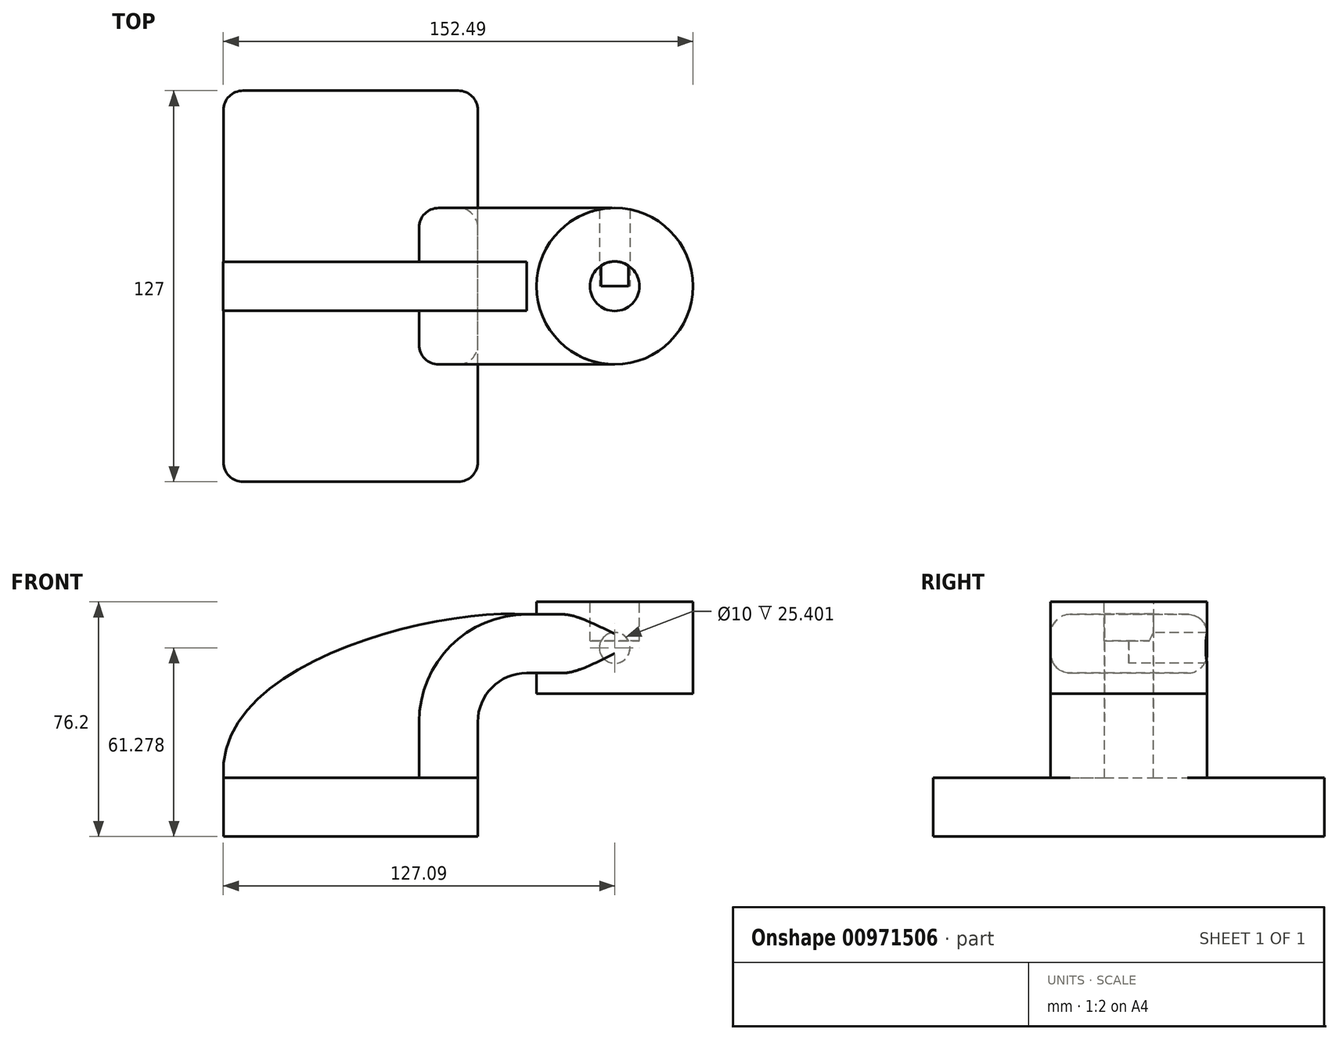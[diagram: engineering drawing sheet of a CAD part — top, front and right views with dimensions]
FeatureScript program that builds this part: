
annotation { "Feature Type Name" : "Feature", "Feature Type Description" : "" }
export const myFeature = defineFeature(function(context is Context, id is Id, definition is map)
    precondition{}
    {
        {
            var Q0;
            Q0=qCreatedBy(makeId("Front.planeOp"),FACE);
            var sketch = newSketch(context, id + "F0", { "sketchPlane" : qUnion([Q0])});
            skLineSegment(sketch, "E0.bottom", {"start": v(0, 0) * mm, "end": v(-82.55, 0) * mm});
            skLineSegment(sketch, "E0.top", {"start": v(0, 19.05) * mm, "end": v(-82.55, 19.05) * mm});
            skLineSegment(sketch, "E0.left", {"start": v(0, 0) * mm, "end": v(0, 19.05) * mm});
            skLineSegment(sketch, "E0.right", {"start": v(-82.55, 0) * mm, "end": v(-82.55, 19.05) * mm});
            skLineSegment(sketch, "E1", {"start": v(0, 19.05) * mm, "end": v(0, 37.22) * mm});
            skArc(sketch, "E2", {"start": v(15.88, 53.1) * mm, "mid": v(4.65, 48.44) * mm, "end": v(0, 37.22) * mm});
            skLineSegment(sketch, "E3", {"start": v(15.88, 53.1) * mm, "end": v(64.16, 53.1) * mm});
            skLineSegment(sketch, "E4.bottom", {"start": v(69.85, 46.35) * mm, "end": v(19.05, 46.35) * mm});
            skLineSegment(sketch, "E4.top", {"start": v(69.85, 76.2) * mm, "end": v(19.05, 76.2) * mm});
            skLineSegment(sketch, "E4.left", {"start": v(69.85, 46.35) * mm, "end": v(69.85, 76.2) * mm});
            skLineSegment(sketch, "E4.right", {"start": v(19.05, 46.35) * mm, "end": v(19.05, 76.2) * mm});
            skPoint(sketch, "E4.middle", {"position": v(44.45, 61.28) * mm});
            skLineSegment(sketch, "E5.0", {"start": v(15.88, 72.14) * mm, "end": v(64.16, 72.14) * mm});
            skArc(sketch, "E5.1", {"start": v(15.88, 72.14) * mm, "mid": v(-8.82, 61.91) * mm, "end": v(-19.05, 37.22) * mm});
            skLineSegment(sketch, "E5.2", {"start": v(-19.05, 19.05) * mm, "end": v(-19.05, 37.22) * mm});
            skLineSegment(sketch, "E6", {"start": v(44.45, 46.35) * mm, "end": v(44.45, 76.2) * mm});
            skFitSpline(sketch, "E7", {"points": [v(-82.55, 19.05) * mm, v(15.88, 72.14) * mm], "startDerivative": vector(-9.17, 113.87) * mm, "endDerivative": vector(84.95, -6.67) * mm});
            skSolve(sketch);
        }
        {
            var Q0;
            Q0=makeQuery(id+"F0.imprint","IMPRINT",FACE,{"disambiguationData":[TD([[makeQuery(id+"F0.imprint","IMPRINT",EDGE,{"derivedFrom":sQuery(id+"F0.wireOp",EDGE,"E0.bottom")}),-1.0]])]});
            extrude(context, id + "F1", {"entities" : qUnion([Q0]), "endBound" : BoundingType.SYMMETRIC, "depth" : 127 * mm, "offsetDistance" : 25.4 * mm});
        }
        {
            var Q0;
            {var subQ4=sQuery(id+"F0.wireOp",EDGE,"E1");Q0=makeQuery(id+"F0.imprint","IMPRINT",FACE,{"disambiguationData":[TD([[makeQuery(id+"F0.imprint","IMPRINT",EDGE,{"derivedFrom":subQ4}),1.0]])]});}
            var Q1;
            {var subQ0=sQuery(id+"F0.wireOp",EDGE,"E4.right");var subQ1=sQuery(id+"F0.wireOp",EDGE,"E3");var subQ2=makeQuery(id+"F0.imprint","INTERSECT",VERTEX,{"derivedFrom":[subQ1,subQ0]});Q1=makeQuery(id+"F0.imprint","IMPRINT",FACE,{"disambiguationData":[TD([[makeQuery(id+"F0.imprint","IMPRINT",EDGE,{"disambiguationData":[TD([[subQ2,-1.0]])],"derivedFrom":subQ1}),1.0]])]});}
            extrude(context, id + "F2", {"entities" : qUnion([Q0, Q1]), "operationType" : NewBodyOperationType.ADD, "endBound" : BoundingType.SYMMETRIC, "depth" : 50.8 * mm, "offsetDistance" : 25.4 * mm});
        }
        {
            var Q0;
            Q0=makeQuery(id+"F0.imprint","IMPRINT",FACE,{"disambiguationData":[TD([[makeQuery(id+"F0.imprint","IMPRINT",EDGE,{"derivedFrom":sQuery(id+"F0.wireOp",EDGE,"E5.1")}),-1.0]])]});
            extrude(context, id + "F3", {"entities" : qUnion([Q0]), "operationType" : NewBodyOperationType.ADD, "endBound" : BoundingType.SYMMETRIC, "depth" : 15.88 * mm, "offsetDistance" : 25.4 * mm});
        }
        {
            var Q0;
            {var subQ0=sQuery(id+"F0.wireOp",EDGE,"E4.left");Q0=makeQuery(id+"F0.imprint","IMPRINT",FACE,{"disambiguationData":[TD([[makeQuery(id+"F0.imprint","IMPRINT",EDGE,{"derivedFrom":subQ0}),1.0]])]});}
            var Q1;
            Q1=sQuery(id+"F0.wireOp",EDGE,"E6");
            revolve(context, id + "F4", {"operationType" : NewBodyOperationType.ADD, "surfaceOperationType" : NewSurfaceOperationType.NEW, "entities" : qUnion([Q0]), "axis" : qUnion([Q1]), "revolveType" : RevolveType.FULL});
        }
        {
            var Q0;
            Q0=makeQuery(id+"F1.opExtrude","CAP_EDGE",EDGE,{"disambiguationData":[OSD([sQuery(id+"F0.wireOp",EDGE,"E0.right")])],"isStart":false});
            var Q1;
            Q1=makeQuery(id+"F1.opExtrude","CAP_EDGE",EDGE,{"disambiguationData":[OSD([sQuery(id+"F0.wireOp",EDGE,"E0.left")])],"isStart":false});
            var Q2;
            Q2=makeQuery(id+"F1.opExtrude","CAP_EDGE",EDGE,{"disambiguationData":[OSD([sQuery(id+"F0.wireOp",EDGE,"E0.right")])],"isStart":true});
            var Q3;
            Q3=makeQuery(id+"F1.opExtrude","CAP_EDGE",EDGE,{"disambiguationData":[OSD([sQuery(id+"F0.wireOp",EDGE,"E0.left")])],"isStart":true});
            var Q4;
            Q4=makeQuery(id+"F2.opExtrude","CAP_EDGE",EDGE,{"disambiguationData":[OSD([sQuery(id+"F0.wireOp",EDGE,"E5.2")])],"isStart":true});
            var Q5;
            Q5=makeQuery(id+"F2.opExtrude","CAP_EDGE",EDGE,{"disambiguationData":[OSD([sQuery(id+"F0.wireOp",EDGE,"E5.2")])],"isStart":false});
            var Q6;
            Q6=makeQuery(id+"F2.opExtrude","CAP_EDGE",EDGE,{"disambiguationData":[OSD([sQuery(id+"F0.wireOp",EDGE,"E1")])],"isStart":true});
            var Q7;
            Q7=makeQuery(id+"F2.opExtrude","CAP_EDGE",EDGE,{"disambiguationData":[OSD([sQuery(id+"F0.wireOp",EDGE,"E1")])],"isStart":false});
            fillet(context, id + "F5", {"entities" : qUnion([Q0, Q1, Q2, Q3, Q4, Q5, Q6, Q7]), "radius" : 6.35 * mm, "tangentPropagation" : true, "allowEdgeOverflow" : false});
        }
        {
            var Q0;
            Q0=makeQuery(id+"F4.opRevolve","SWEPT_FACE",FACE,{"disambiguationData":[OSD([sQuery(id+"F0.wireOp",EDGE,"E4.top")])]});
            var sketch = newSketch(context, id + "F6", { "sketchPlane" : qUnion([Q0])});
            skCircle(sketch, "E8", {"center": v(44.45, 0) * mm, "radius": 8.03 * mm});
            skSolve(sketch);
        }
        {
            var Q0;
            Q0 = qSketchRegion(id + "F6", true);
            extrude(context, id + "F7", {"entities" : qUnion([Q0]), "operationType" : NewBodyOperationType.REMOVE, "oppositeDirection" : true, "depth" : 12.7 * mm, "offsetDistance" : 25.4 * mm});
        }
        {
            var Q0;
            Q0=sQuery(id+"F0.wireOp",VERTEX,"E4.middle");
            var Q1;
            Q1=makeQuery(id+"F1.opExtrude","SWEPT_BODY",BODY,{"disambiguationData":[OSD([sQuery(id+"F0.wireOp",EDGE,"E0.bottom"),sQuery(id+"F0.wireOp",EDGE,"E0.top"),sQuery(id+"F0.wireOp",EDGE,"E0.left"),sQuery(id+"F0.wireOp",EDGE,"E0.right")])]});
            hole(context, id + "F8", {"style" : HoleStyle.SIMPLE, "endStyle" : HoleEndStyle.THROUGH, "holeDiameter" : 10 * mm, "majorDiameter" : 6.35 * mm, "isTappedThrough" : true, "tappedDepth" : 12.7 * mm, "tapClearance" : 3, "locations" : qUnion([Q0]), "scope" : qUnion([Q1])});
        }
    });
